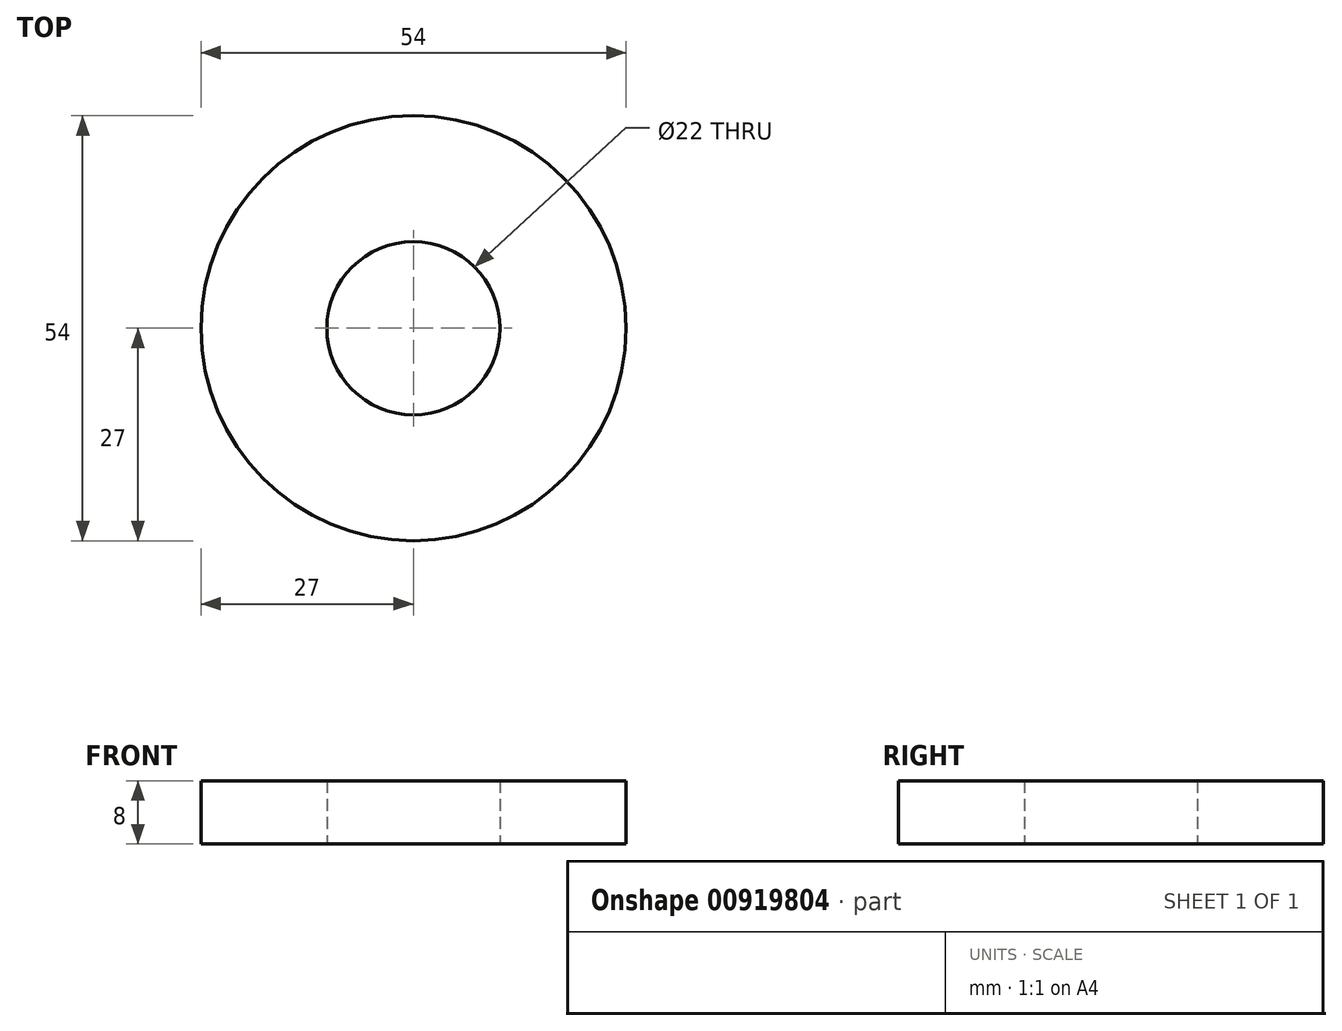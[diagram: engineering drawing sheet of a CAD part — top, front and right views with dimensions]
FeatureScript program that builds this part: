
annotation { "Feature Type Name" : "Feature", "Feature Type Description" : "" }
export const myFeature = defineFeature(function(context is Context, id is Id, definition is map)
    precondition{}
    {
        {
            var Q0;
            Q0=qCreatedBy(makeId("Top.planeOp"),FACE);
            var sketch = newSketch(context, id + "F0", { "sketchPlane" : qUnion([Q0])});
            skCircle(sketch, "E0", {"center": v(0, 0) * mm, "radius": 11 * mm});
            skCircle(sketch, "E1", {"center": v(0, 0) * mm, "radius": 27 * mm});
            skSolve(sketch);
        }
        {
            var Q0;
            Q0=makeQuery(id+"F0.imprint","IMPRINT",FACE,{"disambiguationData":[TD([[makeQuery(id+"F0.imprint","IMPRINT",EDGE,{"derivedFrom":sQuery(id+"F0.wireOp",EDGE,"E0")}),-1.0]])]});
            extrude(context, id + "F1", {"entities" : qUnion([Q0]), "depth" : 8 * mm, "offsetDistance" : 25 * mm});
        }
    });
